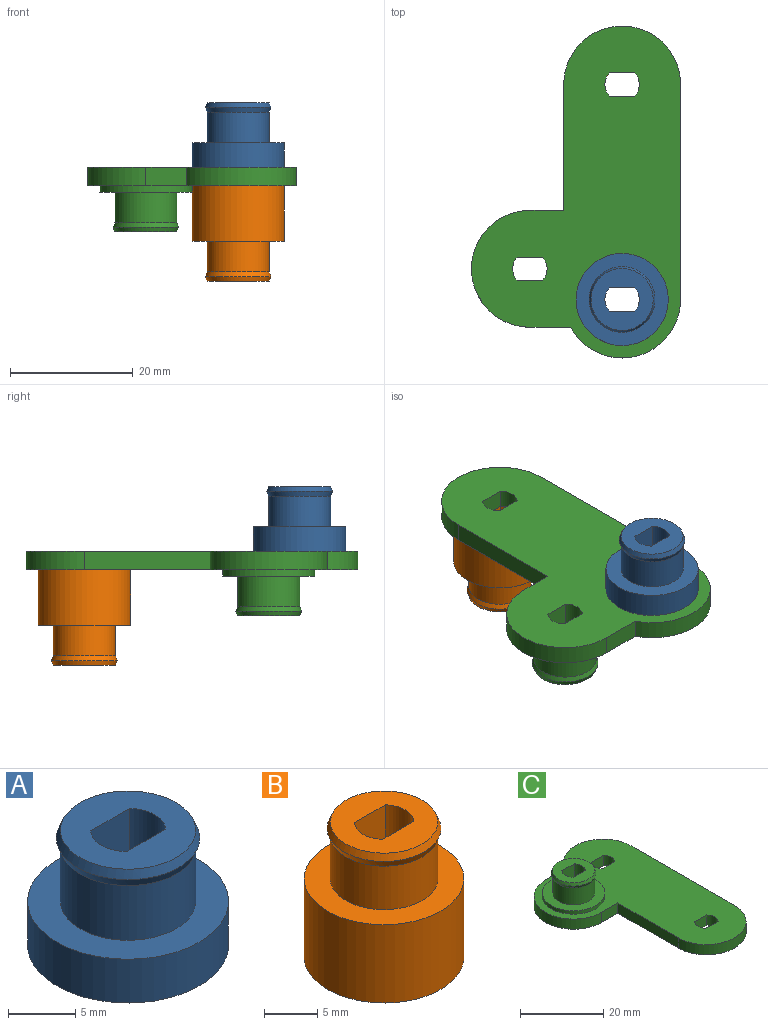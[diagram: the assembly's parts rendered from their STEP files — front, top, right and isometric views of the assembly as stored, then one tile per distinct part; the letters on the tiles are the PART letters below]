
ASSEMBLY  parts=3 mates=2
PART A: 11 faces, bbox 15x15x10.5 mm
  f0: plane 15x15mm, normal (0,0,1), area 96.6mm2, adj f4,f7
  f1: cylinder r=2.8mm len=10.5mm, axis (0,0,-1), area 43.9mm2, adj f2,f5,f6,f8
  f2: plane 10.5x4.11mm, normal (0,-1,0), area 43.2mm2, adj f1,f3,f6,f8
  f3: cylinder r=2.8mm len=10.5mm, axis (0,0,-1), area 43.9mm2, adj f2,f5,f6,f8
  f4: cylinder r=7.5mm len=15mm, axis (0,0,-1), area 188.5mm2, adj f0,f6
  f5: plane 10.5x4.11mm, normal (0,1,0), area 43.2mm2, adj f1,f3,f6,f8
  f6: plane 15x15mm, normal (0,0,-1), area 157.2mm2, adj f1,f2,f3,f4,f5
  f7: cylinder r=5.05mm len=10.1mm, axis (0,0,-1), area 158.7mm2, adj f0,f9
  f8: plane 10.1x10.1mm, normal (0,0,1), area 60.6mm2, adj f1,f2,f3,f5,f10
  f9: cone r=5.35mm half-angle=21.8deg, axis (0,0,1), area 26.4mm2, adj f7,f10
  f10: cone r=5.05mm half-angle=21.8deg, axis (0,0,-1), area 26.4mm2, adj f8,f9
PART B: 11 faces, bbox 15x15x15.5 mm
  f0: plane 15x15mm, normal (0,0,1), area 96.6mm2, adj f4,f7
  f1: cylinder r=2.8mm len=15.5mm, axis (0,0,-1), area 64.7mm2, adj f2,f5,f6,f8
  f2: plane 15.5x4.11mm, normal (0,-1,0), area 63.8mm2, adj f1,f3,f6,f8
  f3: cylinder r=2.8mm len=15.5mm, axis (0,0,-1), area 64.7mm2, adj f2,f5,f6,f8
  f4: cylinder r=7.5mm len=15mm, axis (0,0,-1), area 424.1mm2, adj f0,f6
  f5: plane 15.5x4.11mm, normal (0,1,0), area 63.8mm2, adj f1,f3,f6,f8
  f6: plane 15x15mm, normal (0,0,-1), area 157.2mm2, adj f1,f2,f3,f4,f5
  f7: cylinder r=5.05mm len=10.1mm, axis (0,0,-1), area 158.7mm2, adj f0,f9
  f8: plane 10.1x10.1mm, normal (0,0,1), area 60.6mm2, adj f1,f2,f3,f5,f10
  f9: cone r=5.35mm half-angle=21.8deg, axis (0,0,1), area 26.4mm2, adj f7,f10
  f10: cone r=5.05mm half-angle=21.8deg, axis (0,0,-1), area 26.4mm2, adj f8,f9
PART C: 27 faces, bbox 34x54x10.5 mm
  f0: cylinder r=9.5mm len=19mm, axis (0,0,-1), area 89.5mm2, adj f1,f6,f7,f8
  f1: plane 35x3mm, normal (1,0,0), area 105mm2, adj f0,f2,f7,f8
  f2: cylinder r=9.5mm len=17.87mm, axis (0,0,-1), area 75.5mm2, adj f1,f3,f7,f8
  f3: plane 6.63x3mm, normal (0,1,0), area 19.9mm2, adj f2,f4,f7,f8
  f4: cylinder r=9.5mm len=19mm, axis (0,0,-1), area 89.5mm2, adj f3,f5,f7,f8
  f5: plane 5.5x3mm, normal (0,-1,0), area 16.5mm2, adj f4,f6,f7,f8
  f6: plane 20.5x3mm, normal (-1,0,0), area 61.5mm2, adj f0,f5,f7,f8
  f7: plane 54x34mm, normal (0,0,1), area 980.7mm2, adj f0,f1,f2,f3,f4,f5,f6,f14
  f8: plane 54x34mm, normal (0,0,-1), area 1137.9mm2, adj f0,f1,f2,f3,f4,f5,f6,f10
  f9: cylinder r=5.05mm len=10.1mm, axis (0,0,-1), area 158.7mm2, adj f15,f17
  f10: cylinder r=2.8mm len=10.5mm, axis (0,0,-1), area 43.9mm2, adj f8,f11,f13,f16
  f11: plane 10.5x4.11mm, normal (0,-1,0), area 43.2mm2, adj f8,f10,f12,f16
  f12: cylinder r=2.8mm len=10.5mm, axis (0,0,-1), area 43.9mm2, adj f8,f11,f13,f16
  f13: plane 10.5x4.11mm, normal (0,1,0), area 43.2mm2, adj f8,f10,f12,f16
  f14: cylinder r=7.5mm len=15mm, axis (0,0,-1), area 47.1mm2, adj f7,f15
  f15: plane 15x15mm, normal (0,0,1), area 96.6mm2, adj f9,f14
  f16: plane 10.1x10.1mm, normal (0,0,1), area 60.6mm2, adj f10,f11,f12,f13,f18
  f17: cone r=5.35mm half-angle=21.8deg, axis (0,0,1), area 26.4mm2, adj f9,f18
  f18: cone r=5.05mm half-angle=21.8deg, axis (0,0,-1), area 26.4mm2, adj f16,f17
  f19: plane 4.11x3mm, normal (0,-1,0), area 12.3mm2, adj f7,f8,f20,f22
  f20: cylinder r=2.8mm len=3.8mm, axis (0,0,-1), area 12.5mm2, adj f7,f8,f19,f21
  f21: plane 4.11x3mm, normal (0,1,0), area 12.3mm2, adj f7,f8,f20,f22
  f22: cylinder r=2.8mm len=3.8mm, axis (0,0,-1), area 12.5mm2, adj f7,f8,f19,f21
  f23: plane 4.11x3mm, normal (0,-1,0), area 12.3mm2, adj f7,f8,f24,f26
  f24: cylinder r=2.8mm len=3.8mm, axis (0,0,-1), area 12.5mm2, adj f7,f8,f23,f25
  f25: plane 4.11x3mm, normal (0,1,0), area 12.3mm2, adj f7,f8,f24,f26
  f26: cylinder r=2.8mm len=3.8mm, axis (0,0,-1), area 12.5mm2, adj f7,f8,f23,f25
PLACE A t=(30.45,23.16,5.62)mm
PLACE B rot(axis=(1,0,0),180deg) t=(30.45,58.16,2.62)mm
PLACE C rot(axis=(1,0,0),180deg) t=(10.45,43.16,5.62)mm
MATE fastened A.f4 <-> C.f2  axis (0,0,-1) through (30.45,23.16,5.62)mm
MATE fastened B.f4 <-> C.f0  axis (0,0,1) through (30.45,58.16,2.62)mm
